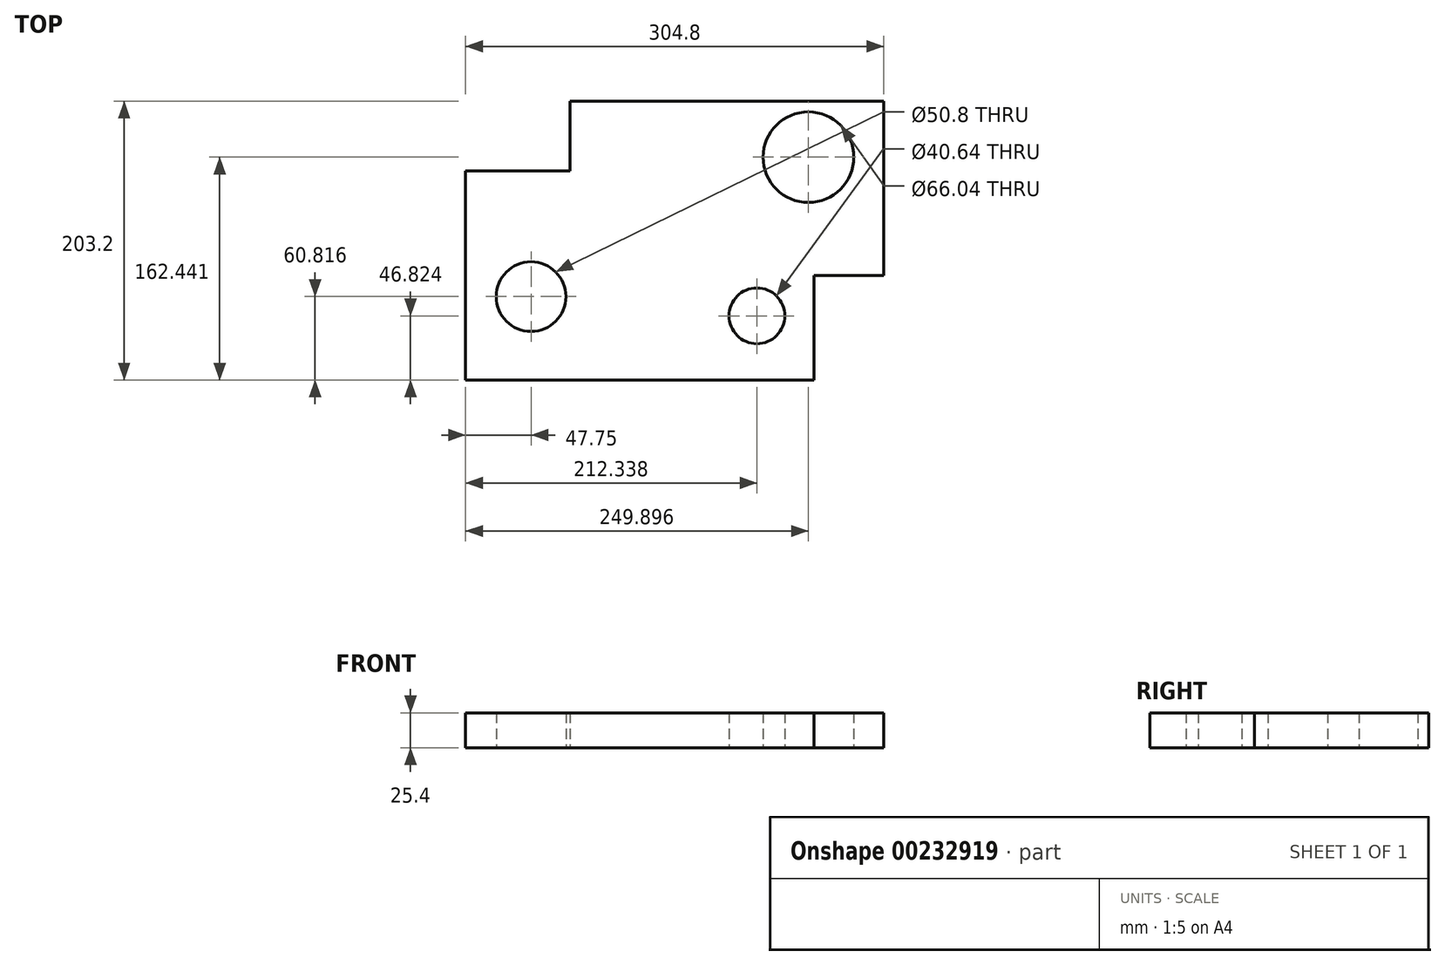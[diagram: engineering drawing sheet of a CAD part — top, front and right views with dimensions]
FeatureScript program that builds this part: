
annotation { "Feature Type Name" : "Feature", "Feature Type Description" : "" }
export const myFeature = defineFeature(function(context is Context, id is Id, definition is map)
    precondition{}
    {
        {
            var Q0;
            Q0=qCreatedBy(makeId("Top.planeOp"),FACE);
            var sketch = newSketch(context, id + "F0", { "sketchPlane" : qUnion([Q0])});
            skLineSegment(sketch, "E0", {"start": v(-120.75, -77.9) * mm, "end": v(133.25, -77.9) * mm});
            skLineSegment(sketch, "E1", {"start": v(-120.75, -77.9) * mm, "end": v(-120.75, 74.5) * mm});
            skLineSegment(sketch, "E2", {"start": v(-120.75, 74.5) * mm, "end": v(-44.55, 74.5) * mm});
            skLineSegment(sketch, "E3", {"start": v(-44.55, 74.5) * mm, "end": v(-44.55, 125.3) * mm});
            skLineSegment(sketch, "E4", {"start": v(-44.55, 125.3) * mm, "end": v(184.05, 125.3) * mm});
            skLineSegment(sketch, "E5", {"start": v(184.05, 125.3) * mm, "end": v(184.05, -1.7) * mm});
            skLineSegment(sketch, "E6", {"start": v(184.05, -1.7) * mm, "end": v(133.25, -1.7) * mm});
            skLineSegment(sketch, "E7", {"start": v(133.25, -1.7) * mm, "end": v(133.25, -77.9) * mm});
            skCircle(sketch, "E8", {"center": v(-73, -17.08) * mm, "radius": 25.4 * mm});
            skCircle(sketch, "E9", {"center": v(91.59, -31.08) * mm, "radius": 20.32 * mm});
            skCircle(sketch, "E10", {"center": v(129.15, 84.54) * mm, "radius": 33.02 * mm});
            skSolve(sketch);
        }
        {
            var Q0;
            Q0 = qSketchRegion(id + "F0", true);
            extrude(context, id + "F1", {"entities" : qUnion([Q0]), "depth" : 25.4 * mm});
        }
    });
